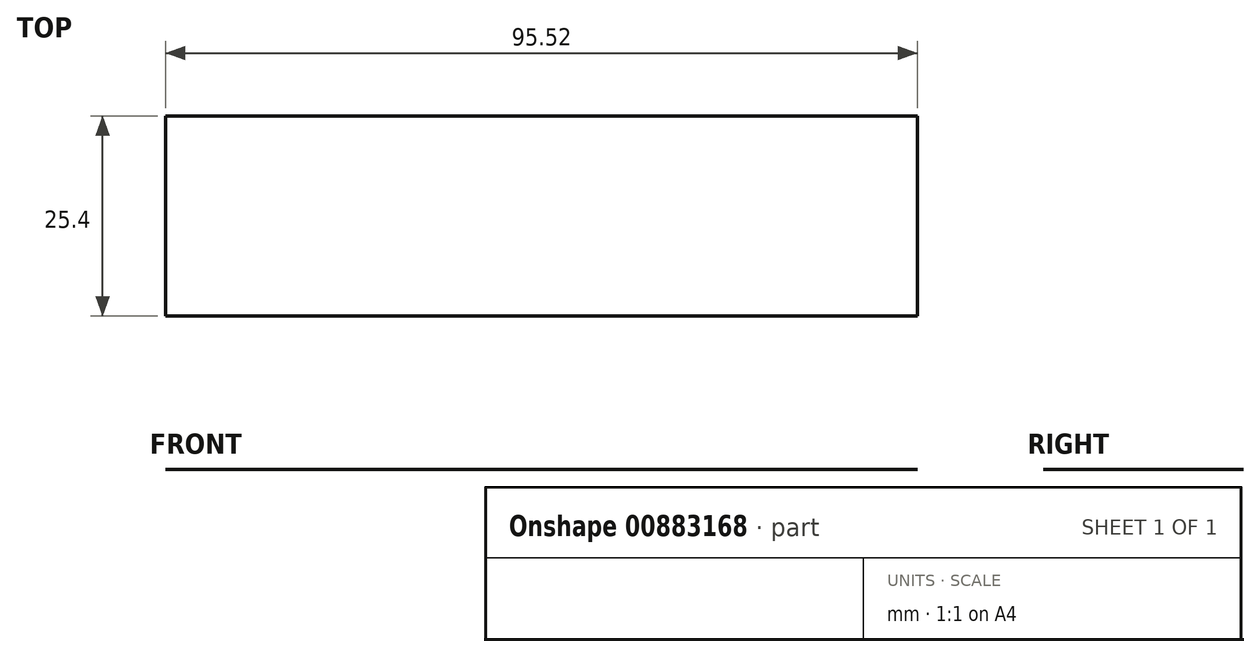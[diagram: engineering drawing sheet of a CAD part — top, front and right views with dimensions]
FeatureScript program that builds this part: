
annotation { "Feature Type Name" : "Feature", "Feature Type Description" : "" }
export const myFeature = defineFeature(function(context is Context, id is Id, definition is map)
    precondition{}
    {
        {
            var Q0;
            Q0=qCreatedBy(makeId("Front.planeOp"),FACE);
            var sketch = newSketch(context, id + "F0", { "sketchPlane" : qUnion([Q0])});
            skLineSegment(sketch, "E0.bottom", {"start": v(-50.75, 46.4) * mm, "end": v(44.77, 46.4) * mm});
            skLineSegment(sketch, "E0.top", {"start": v(-50.75, -49.67) * mm, "end": v(44.77, -49.67) * mm});
            skLineSegment(sketch, "E0.left", {"start": v(-50.75, 46.4) * mm, "end": v(-50.75, -49.67) * mm});
            skLineSegment(sketch, "E0.right", {"start": v(44.77, 46.4) * mm, "end": v(44.77, -49.67) * mm});
            skLineSegment(sketch, "E1.bottom", {"start": v(-3, 46.4) * mm, "end": v(-50.75, 46.4) * mm, "construction": true});
            skLineSegment(sketch, "E1.top", {"start": v(-3, -1.63) * mm, "end": v(-50.75, -1.63) * mm, "construction": true});
            skLineSegment(sketch, "E1.left", {"start": v(-3, 46.4) * mm, "end": v(-3, -1.63) * mm, "construction": true});
            skLineSegment(sketch, "E1.right", {"start": v(-50.75, 46.4) * mm, "end": v(-50.75, -1.63) * mm, "construction": true});
            skSolve(sketch);
        }
        {
            var Q0;
            Q0=sQuery(id+"F0.wireOp",EDGE,"E0.bottom");
            extrude(context, id + "F1", {"bodyType" : ToolBodyType.SURFACE, "surfaceEntities" : qUnion([Q0]), "depth" : 25.4 * mm, "offsetDistance" : 25.4 * mm});
        }
    });
